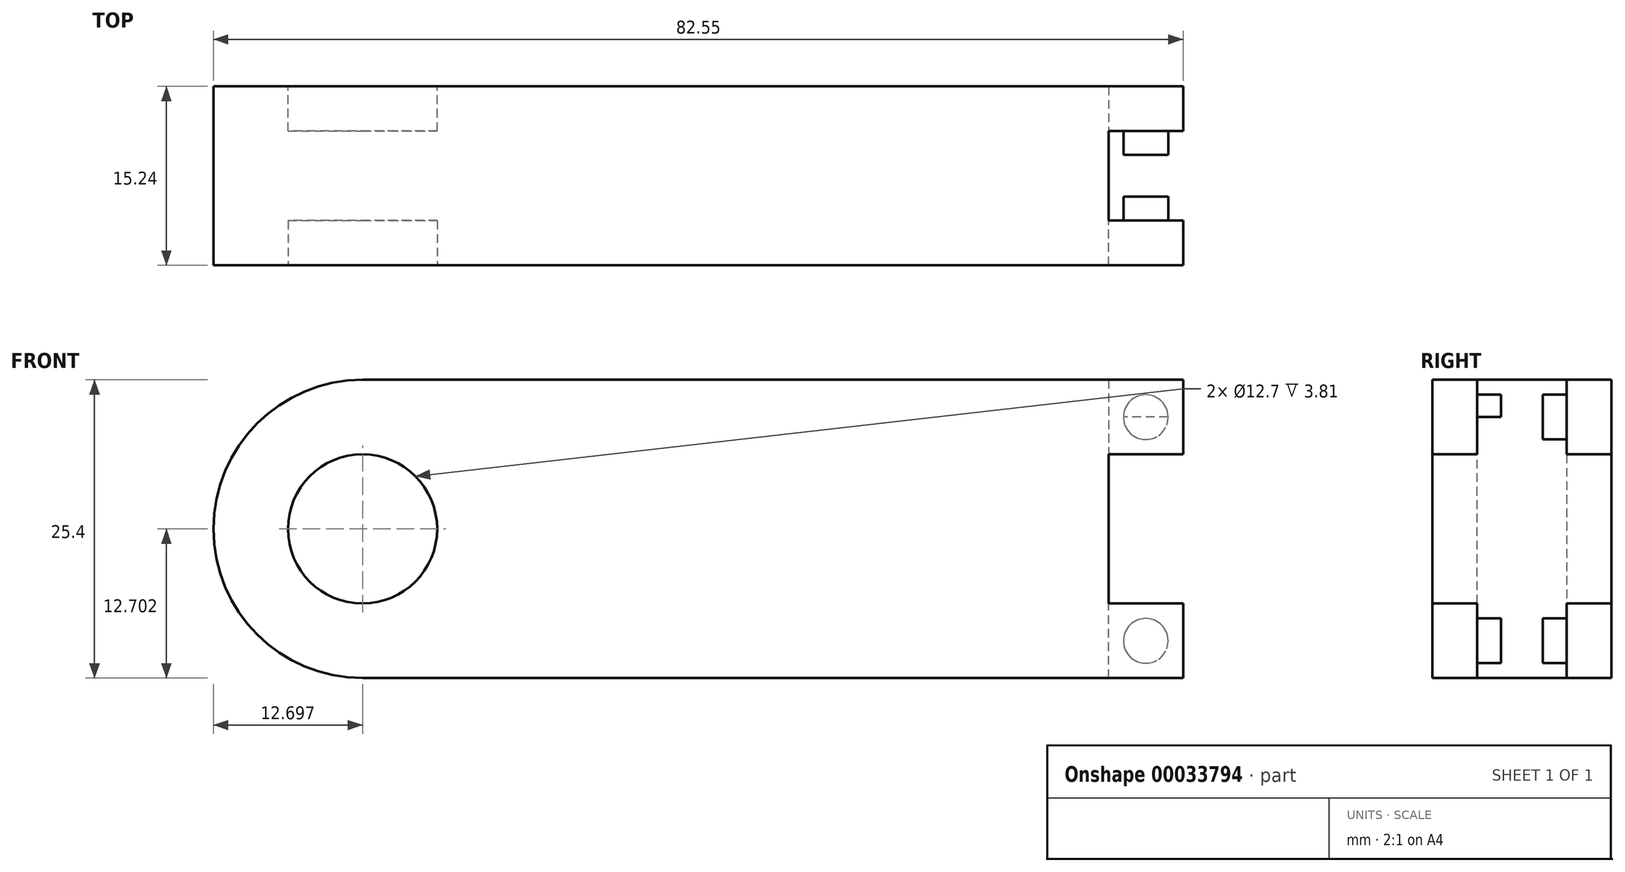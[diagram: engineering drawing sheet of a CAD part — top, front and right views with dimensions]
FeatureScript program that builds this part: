
annotation { "Feature Type Name" : "Feature", "Feature Type Description" : "" }
export const myFeature = defineFeature(function(context is Context, id is Id, definition is map)
    precondition{}
    {
        {
            var Q0;
            Q0=qCreatedBy(makeId("Front.planeOp"),FACE);
            var sketch = newSketch(context, id + "F0", { "sketchPlane" : qUnion([Q0])});
            skLineSegment(sketch, "E0.bottom", {"start": v(16.69, 10.43) * mm, "end": v(92.89, 10.43) * mm});
            skLineSegment(sketch, "E0.top", {"start": v(16.69, -14.97) * mm, "end": v(92.89, -14.97) * mm});
            skLineSegment(sketch, "E0.left", {"start": v(16.69, 10.43) * mm, "end": v(16.69, -14.97) * mm});
            skLineSegment(sketch, "E0.right", {"start": v(92.89, 10.43) * mm, "end": v(92.89, -14.97) * mm});
            skCircle(sketch, "E1", {"center": v(29.39, -2.27) * mm, "radius": 12.7 * mm});
            skCircle(sketch, "E2", {"center": v(29.39, -2.27) * mm, "radius": 6.35 * mm});
            skSolve(sketch);
        }
        {
            var Q0;
            Q0=makeQuery(id+"F0.imprint","IMPRINT",FACE,{"disambiguationData":[TD([[makeQuery(id+"F0.imprint","IMPRINT",EDGE,{"derivedFrom":sQuery(id+"F0.wireOp",EDGE,"E2")}),-1.0]])]});
            var Q1;
            Q1=makeQuery(id+"F0.imprint","IMPRINT",FACE,{"disambiguationData":[TD([[makeQuery(id+"F0.imprint","IMPRINT",EDGE,{"derivedFrom":sQuery(id+"F0.wireOp",EDGE,"E2")}),1.0]])]});
            var Q2;
            {var subQ5=sQuery(id+"F0.wireOp",EDGE,"E0.right");Q2=makeQuery(id+"F0.imprint","IMPRINT",FACE,{"disambiguationData":[TD([[makeQuery(id+"F0.imprint","IMPRINT",EDGE,{"derivedFrom":subQ5}),-1.0]])]});}
            extrude(context, id + "F1", {"entities" : qUnion([Q0, Q1, Q2]), "oppositeDirection" : true, "depth" : 25.4 * mm});
        }
        {
            var Q0;
            Q0=makeQuery(id+"F1.opExtrude","CAP_FACE",FACE,{"disambiguationData":[OSD([sQuery(id+"F0.wireOp",EDGE,"E0.bottom"),sQuery(id+"F0.wireOp",EDGE,"E0.top"),sQuery(id+"F0.wireOp",EDGE,"E0.right"),sQuery(id+"F0.wireOp",EDGE,"E1")])],"isStart":false});
            var sketch = newSketch(context, id + "F2", { "sketchPlane" : qUnion([Q0])});
            skCircle(sketch, "E3", {"center": v(-29.39, -2.27) * mm, "radius": 12.7 * mm});
            skCircle(sketch, "E4", {"center": v(-29.39, -2.27) * mm, "radius": 6.35 * mm});
            skSolve(sketch);
        }
        {
            var Q0;
            {var subQ0=sQuery(id+"F2.wireOp",EDGE,"E3");Q0=makeQuery(id+"F2.imprint","IMPRINT",FACE,{"disambiguationData":[TD([[makeQuery(id+"F2.imprint","IMPRINT",EDGE,{"disambiguationData":[OD(0.0)],"derivedFrom":subQ0}),1.0]])]});}
            var Q1;
            Q1=makeQuery(id+"F2.imprint","IMPRINT",FACE,{"disambiguationData":[TD([[makeQuery(id+"F2.imprint","IMPRINT",EDGE,{"derivedFrom":sQuery(id+"F2.wireOp",EDGE,"E4")}),1.0]])]});
            extrude(context, id + "F3", {"entities" : qUnion([Q0, Q1]), "operationType" : NewBodyOperationType.REMOVE, "endBound" : BoundingType.UP_TO_NEXT, "oppositeDirection" : true, "depth" : 25.4 * mm});
        }
        {
            var Q0;
            {var subQ0=sQuery(id+"F2.wireOp",EDGE,"E3");Q0=makeQuery(id+"F2.imprint","IMPRINT",FACE,{"disambiguationData":[TD([[makeQuery(id+"F2.imprint","IMPRINT",EDGE,{"disambiguationData":[OD(0.0)],"derivedFrom":subQ0}),1.0]])]});}
            extrude(context, id + "F4", {"entities" : qUnion([Q0]), "operationType" : NewBodyOperationType.ADD, "oppositeDirection" : true, "depth" : 5.08 * mm});
        }
        {
            var Q0;
            Q0=makeQuery(id+"F2.imprint","IMPRINT",FACE,{"disambiguationData":[TD([[makeQuery(id+"F2.imprint","IMPRINT",EDGE,{"derivedFrom":sQuery(id+"F2.wireOp",EDGE,"E4")}),1.0]])]});
            extrude(context, id + "F5", {"entities" : qUnion([Q0]), "operationType" : NewBodyOperationType.ADD, "oppositeDirection" : true, "depth" : 8.9 * mm});
        }
        {
            var Q0;
            {var subQ0=sQuery(id+"F2.wireOp",EDGE,"E3");Q0=makeQuery(id+"F2.imprint","IMPRINT",FACE,{"disambiguationData":[TD([[makeQuery(id+"F2.imprint","IMPRINT",EDGE,{"disambiguationData":[OD(0.0)],"derivedFrom":subQ0}),1.0]])]});}
            var Q1;
            Q1=makeQuery(id+"F2.imprint","IMPRINT",FACE,{"disambiguationData":[TD([[makeQuery(id+"F2.imprint","IMPRINT",EDGE,{"derivedFrom":sQuery(id+"F2.wireOp",EDGE,"E4")}),1.0]])]});
            extrude(context, id + "F6", {"entities" : qUnion([Q0, Q1]), "operationType" : NewBodyOperationType.ADD, "oppositeDirection" : true, "depth" : 20.32 * mm});
        }
        {
            var Q0;
            Q0=makeQuery(id+"F1.opExtrude","CAP_FACE",FACE,{"disambiguationData":[OSD([sQuery(id+"F0.wireOp",EDGE,"E0.bottom"),sQuery(id+"F0.wireOp",EDGE,"E0.top"),sQuery(id+"F0.wireOp",EDGE,"E0.right"),sQuery(id+"F0.wireOp",EDGE,"E1")])],"isStart":true});
            extrude(context, id + "F7", {"entities" : qUnion([Q0]), "operationType" : NewBodyOperationType.REMOVE, "oppositeDirection" : true, "depth" : 10.16 * mm});
        }
        {
            var Q0;
            Q0=makeQuery(id+"F6.opExtrude","CAP_FACE",FACE,{"disambiguationData":[OSD([sQuery(id+"F2.wireOp",EDGE,"E3")])],"isStart":false});
            extrude(context, id + "F8", {"entities" : qUnion([Q0]), "operationType" : NewBodyOperationType.REMOVE, "oppositeDirection" : true, "depth" : 5.08 * mm});
        }
        {
            var Q0;
            Q0=makeQuery(id+"F0.imprint","IMPRINT",FACE,{"disambiguationData":[TD([[makeQuery(id+"F0.imprint","IMPRINT",EDGE,{"derivedFrom":sQuery(id+"F0.wireOp",EDGE,"E2")}),1.0]])]});
            extrude(context, id + "F9", {"entities" : qUnion([Q0]), "operationType" : NewBodyOperationType.REMOVE, "oppositeDirection" : true, "depth" : 13.97 * mm});
        }
        {
            var Q0;
            Q0=makeQuery(id+"F2.imprint","IMPRINT",FACE,{"disambiguationData":[TD([[makeQuery(id+"F2.imprint","IMPRINT",EDGE,{"derivedFrom":sQuery(id+"F2.wireOp",EDGE,"E4")}),1.0]])]});
            extrude(context, id + "F10", {"entities" : qUnion([Q0]), "operationType" : NewBodyOperationType.REMOVE, "oppositeDirection" : true, "depth" : 3.8 * mm});
        }
        {
            var Q0;
            Q0=makeQuery(id+"F1.opExtrude","SWEPT_FACE",FACE,{"disambiguationData":[OSD([sQuery(id+"F0.wireOp",EDGE,"E0.right")])]});
            var sketch = newSketch(context, id + "F11", { "sketchPlane" : qUnion([Q0])});
            skLineSegment(sketch, "E5.bottom", {"start": v(10.16, 10.43) * mm, "end": v(13.97, 10.43) * mm});
            skLineSegment(sketch, "E5.top", {"start": v(10.16, 4.08) * mm, "end": v(13.97, 4.08) * mm});
            skLineSegment(sketch, "E5.left", {"start": v(10.16, 10.43) * mm, "end": v(10.16, 4.08) * mm});
            skLineSegment(sketch, "E5.right", {"start": v(13.97, 10.43) * mm, "end": v(13.97, 4.08) * mm});
            skLineSegment(sketch, "E6.bottom", {"start": v(25.4, 10.43) * mm, "end": v(21.59, 10.43) * mm});
            skLineSegment(sketch, "E6.top", {"start": v(25.4, 4.08) * mm, "end": v(21.59, 4.08) * mm});
            skLineSegment(sketch, "E6.left", {"start": v(25.4, 10.43) * mm, "end": v(25.4, 4.08) * mm});
            skLineSegment(sketch, "E6.right", {"start": v(21.59, 10.43) * mm, "end": v(21.59, 4.08) * mm});
            skLineSegment(sketch, "E7.bottom", {"start": v(10.16, -14.97) * mm, "end": v(13.97, -14.97) * mm});
            skLineSegment(sketch, "E7.top", {"start": v(10.16, -8.62) * mm, "end": v(13.97, -8.62) * mm});
            skLineSegment(sketch, "E7.left", {"start": v(10.16, -14.97) * mm, "end": v(10.16, -8.62) * mm});
            skLineSegment(sketch, "E7.right", {"start": v(13.97, -14.97) * mm, "end": v(13.97, -8.62) * mm});
            skLineSegment(sketch, "E8.bottom", {"start": v(25.4, -14.97) * mm, "end": v(21.59, -14.97) * mm});
            skLineSegment(sketch, "E8.top", {"start": v(25.4, -8.62) * mm, "end": v(21.59, -8.62) * mm});
            skLineSegment(sketch, "E8.left", {"start": v(25.4, -14.97) * mm, "end": v(25.4, -8.62) * mm});
            skLineSegment(sketch, "E8.right", {"start": v(21.59, -14.97) * mm, "end": v(21.59, -8.62) * mm});
            skSolve(sketch);
        }
        {
            var Q0;
            Q0=makeQuery(id+"F11.imprint","IMPRINT",FACE,{"disambiguationData":[TD([[makeQuery(id+"F11.imprint","IMPRINT",EDGE,{"derivedFrom":sQuery(id+"F11.wireOp",EDGE,"E5.bottom")}),1.0]])]});
            var Q1;
            Q1=makeQuery(id+"F11.imprint","IMPRINT",FACE,{"disambiguationData":[TD([[makeQuery(id+"F11.imprint","IMPRINT",EDGE,{"derivedFrom":sQuery(id+"F11.wireOp",EDGE,"E6.bottom")}),1.0]])]});
            var Q2;
            Q2=makeQuery(id+"F11.imprint","IMPRINT",FACE,{"disambiguationData":[TD([[makeQuery(id+"F11.imprint","IMPRINT",EDGE,{"derivedFrom":sQuery(id+"F11.wireOp",EDGE,"E8.bottom")}),-1.0]])]});
            var Q3;
            Q3=makeQuery(id+"F11.imprint","IMPRINT",FACE,{"disambiguationData":[TD([[makeQuery(id+"F11.imprint","IMPRINT",EDGE,{"derivedFrom":sQuery(id+"F11.wireOp",EDGE,"E7.bottom")}),-1.0]])]});
            extrude(context, id + "F12", {"entities" : qUnion([Q0, Q1, Q2, Q3]), "operationType" : NewBodyOperationType.ADD, "depth" : 6.35 * mm});
        }
        {
            var Q0;
            Q0=makeQuery(id+"F12.opExtrude","SWEPT_FACE",FACE,{"disambiguationData":[OSD([sQuery(id+"F11.wireOp",EDGE,"E5.right")])]});
            var sketch = newSketch(context, id + "F13", { "sketchPlane" : qUnion([Q0])});
            skCircle(sketch, "E9", {"center": v(-96.06, 7.26) * mm, "radius": 1.9 * mm});
            skLineSegment(sketch, "E10", {"start": v(-99.24, 7.26) * mm, "end": v(-92.89, 7.26) * mm});
            skLineSegment(sketch, "E11", {"start": v(-96.06, 10.43) * mm, "end": v(-96.06, 4.08) * mm});
            skSolve(sketch);
        }
        {
            var Q0;
            Q0=makeQuery(id+"F12.opExtrude","SWEPT_FACE",FACE,{"disambiguationData":[OSD([sQuery(id+"F11.wireOp",EDGE,"E6.right")])]});
            var sketch = newSketch(context, id + "F14", { "sketchPlane" : qUnion([Q0])});
            skCircle(sketch, "E12", {"center": v(96.06, 7.26) * mm, "radius": 1.9 * mm});
            skLineSegment(sketch, "E13", {"start": v(99.24, 7.26) * mm, "end": v(92.89, 7.26) * mm});
            skLineSegment(sketch, "E14", {"start": v(96.06, 10.43) * mm, "end": v(96.06, 4.08) * mm});
            skSolve(sketch);
        }
        {
            var Q0;
            Q0=makeQuery(id+"F12.opExtrude","SWEPT_FACE",FACE,{"disambiguationData":[OSD([sQuery(id+"F11.wireOp",EDGE,"E7.right")])]});
            var sketch = newSketch(context, id + "F15", { "sketchPlane" : qUnion([Q0])});
            skLineSegment(sketch, "E15", {"start": v(-99.24, -11.8) * mm, "end": v(-92.89, -11.8) * mm});
            skLineSegment(sketch, "E16", {"start": v(-96.06, -8.62) * mm, "end": v(-96.06, -14.97) * mm});
            skCircle(sketch, "E17", {"center": v(-96.06, -11.8) * mm, "radius": 1.9 * mm});
            skSolve(sketch);
        }
        {
            var Q0;
            Q0=makeQuery(id+"F12.opExtrude","SWEPT_FACE",FACE,{"disambiguationData":[OSD([sQuery(id+"F11.wireOp",EDGE,"E8.right")])]});
            var sketch = newSketch(context, id + "F16", { "sketchPlane" : qUnion([Q0])});
            skLineSegment(sketch, "E18", {"start": v(96.06, -14.97) * mm, "end": v(96.06, -8.62) * mm});
            skLineSegment(sketch, "E19", {"start": v(99.24, -11.8) * mm, "end": v(92.89, -11.8) * mm});
            skCircle(sketch, "E20", {"center": v(96.06, -11.8) * mm, "radius": 1.9 * mm});
            skSolve(sketch);
        }
        {
            var Q0;
            {var subQ1=sQuery(id+"F15.wireOp",EDGE,"E16");var subQ3=sQuery(id+"F15.wireOp",EDGE,"E15");var subQ5=makeQuery(id+"F15.imprint","INTERSECT",VERTEX,{"derivedFrom":[subQ3,subQ1]});Q0=makeQuery(id+"F15.imprint","IMPRINT",FACE,{"disambiguationData":[TD([[makeQuery(id+"F15.imprint","IMPRINT",EDGE,{"disambiguationData":[TD([[subQ5,-1.0]])],"derivedFrom":subQ3}),1.0]])]});}
            var Q1;
            {var subQ0=sQuery(id+"F15.wireOp",EDGE,"E17");var subQ3=sQuery(id+"F15.wireOp",EDGE,"E15");var subQ4=makeQuery(id+"F15.imprint","INTERSECT",VERTEX,{"disambiguationData":[OD(0.0)],"derivedFrom":[subQ3,subQ0]});Q1=makeQuery(id+"F15.imprint","IMPRINT",FACE,{"disambiguationData":[TD([[makeQuery(id+"F15.imprint","IMPRINT",EDGE,{"disambiguationData":[TD([[subQ4,-1.0]])],"derivedFrom":subQ3}),1.0]])]});}
            var Q2;
            {var subQ0=sQuery(id+"F15.wireOp",EDGE,"E17");var subQ3=sQuery(id+"F15.wireOp",EDGE,"E15");var subQ4=makeQuery(id+"F15.imprint","INTERSECT",VERTEX,{"disambiguationData":[OD(0.0)],"derivedFrom":[subQ3,subQ0]});Q2=makeQuery(id+"F15.imprint","IMPRINT",FACE,{"disambiguationData":[TD([[makeQuery(id+"F15.imprint","IMPRINT",EDGE,{"disambiguationData":[TD([[subQ4,-1.0]])],"derivedFrom":subQ3}),-1.0]])]});}
            var Q3;
            {var subQ1=sQuery(id+"F15.wireOp",EDGE,"E16");var subQ3=sQuery(id+"F15.wireOp",EDGE,"E15");var subQ5=makeQuery(id+"F15.imprint","INTERSECT",VERTEX,{"derivedFrom":[subQ3,subQ1]});Q3=makeQuery(id+"F15.imprint","IMPRINT",FACE,{"disambiguationData":[TD([[makeQuery(id+"F15.imprint","IMPRINT",EDGE,{"disambiguationData":[TD([[subQ5,-1.0]])],"derivedFrom":subQ3}),-1.0]])]});}
            var Q4;
            {var subQ0=sQuery(id+"F13.wireOp",EDGE,"E11");var subQ3=sQuery(id+"F13.wireOp",EDGE,"E9");var subQ4=makeQuery(id+"F13.imprint","INTERSECT",VERTEX,{"disambiguationData":[OD(0.0)],"derivedFrom":[subQ3,subQ0]});Q4=makeQuery(id+"F13.imprint","IMPRINT",FACE,{"disambiguationData":[TD([[makeQuery(id+"F13.imprint","IMPRINT",EDGE,{"disambiguationData":[TD([[subQ4,-1.0]])],"derivedFrom":subQ3}),1.0]])]});}
            var Q5;
            {var subQ0=sQuery(id+"F13.wireOp",EDGE,"E11");var subQ3=sQuery(id+"F13.wireOp",EDGE,"E9");var subQ4=makeQuery(id+"F13.imprint","INTERSECT",VERTEX,{"disambiguationData":[OD(0.0)],"derivedFrom":[subQ3,subQ0]});Q5=makeQuery(id+"F13.imprint","IMPRINT",FACE,{"disambiguationData":[TD([[makeQuery(id+"F13.imprint","IMPRINT",EDGE,{"disambiguationData":[TD([[subQ4,1.0]])],"derivedFrom":subQ3}),1.0]])]});}
            var Q6;
            {var subQ1=sQuery(id+"F13.wireOp",EDGE,"E10");var subQ3=sQuery(id+"F13.wireOp",EDGE,"E9");var subQ5=makeQuery(id+"F13.imprint","INTERSECT",VERTEX,{"disambiguationData":[OD(1.0)],"derivedFrom":[subQ3,subQ1]});Q6=makeQuery(id+"F13.imprint","IMPRINT",FACE,{"disambiguationData":[TD([[makeQuery(id+"F13.imprint","IMPRINT",EDGE,{"disambiguationData":[TD([[subQ5,-1.0]])],"derivedFrom":subQ3}),1.0]])]});}
            var Q7;
            {var subQ1=sQuery(id+"F13.wireOp",EDGE,"E10");var subQ3=sQuery(id+"F13.wireOp",EDGE,"E9");var subQ5=makeQuery(id+"F13.imprint","INTERSECT",VERTEX,{"disambiguationData":[OD(0.0)],"derivedFrom":[subQ3,subQ1]});Q7=makeQuery(id+"F13.imprint","IMPRINT",FACE,{"disambiguationData":[TD([[makeQuery(id+"F13.imprint","IMPRINT",EDGE,{"disambiguationData":[TD([[subQ5,1.0]])],"derivedFrom":subQ3}),1.0]])]});}
            extrude(context, id + "F17", {"entities" : qUnion([Q0, Q1, Q2, Q3, Q4, Q5, Q6, Q7]), "operationType" : NewBodyOperationType.ADD, "depth" : 2.03 * mm});
        }
        {
            var Q0;
            {var subQ0=sQuery(id+"F14.wireOp",EDGE,"E14");var subQ3=sQuery(id+"F14.wireOp",EDGE,"E12");var subQ4=makeQuery(id+"F14.imprint","INTERSECT",VERTEX,{"disambiguationData":[OD(0.0)],"derivedFrom":[subQ3,subQ0]});Q0=makeQuery(id+"F14.imprint","IMPRINT",FACE,{"disambiguationData":[TD([[makeQuery(id+"F14.imprint","IMPRINT",EDGE,{"disambiguationData":[TD([[subQ4,-1.0]])],"derivedFrom":subQ3}),1.0]])]});}
            var Q1;
            {var subQ0=sQuery(id+"F14.wireOp",EDGE,"E14");var subQ3=sQuery(id+"F14.wireOp",EDGE,"E12");var subQ4=makeQuery(id+"F14.imprint","INTERSECT",VERTEX,{"disambiguationData":[OD(0.0)],"derivedFrom":[subQ3,subQ0]});Q1=makeQuery(id+"F14.imprint","IMPRINT",FACE,{"disambiguationData":[TD([[makeQuery(id+"F14.imprint","IMPRINT",EDGE,{"disambiguationData":[TD([[subQ4,1.0]])],"derivedFrom":subQ3}),1.0]])]});}
            var Q2;
            {var subQ1=sQuery(id+"F14.wireOp",EDGE,"E13");var subQ3=sQuery(id+"F14.wireOp",EDGE,"E12");var subQ5=makeQuery(id+"F14.imprint","INTERSECT",VERTEX,{"disambiguationData":[OD(0.0)],"derivedFrom":[subQ3,subQ1]});Q2=makeQuery(id+"F14.imprint","IMPRINT",FACE,{"disambiguationData":[TD([[makeQuery(id+"F14.imprint","IMPRINT",EDGE,{"disambiguationData":[TD([[subQ5,1.0]])],"derivedFrom":subQ3}),1.0]])]});}
            var Q3;
            {var subQ1=sQuery(id+"F14.wireOp",EDGE,"E13");var subQ3=sQuery(id+"F14.wireOp",EDGE,"E12");var subQ5=makeQuery(id+"F14.imprint","INTERSECT",VERTEX,{"disambiguationData":[OD(1.0)],"derivedFrom":[subQ3,subQ1]});Q3=makeQuery(id+"F14.imprint","IMPRINT",FACE,{"disambiguationData":[TD([[makeQuery(id+"F14.imprint","IMPRINT",EDGE,{"disambiguationData":[TD([[subQ5,-1.0]])],"derivedFrom":subQ3}),1.0]])]});}
            var Q4;
            {var subQ1=sQuery(id+"F16.wireOp",EDGE,"E19");var subQ3=sQuery(id+"F16.wireOp",EDGE,"E18");var subQ5=makeQuery(id+"F16.imprint","INTERSECT",VERTEX,{"derivedFrom":[subQ3,subQ1]});Q4=makeQuery(id+"F16.imprint","IMPRINT",FACE,{"disambiguationData":[TD([[makeQuery(id+"F16.imprint","IMPRINT",EDGE,{"disambiguationData":[TD([[subQ5,-1.0]])],"derivedFrom":subQ3}),1.0]])]});}
            var Q5;
            {var subQ1=sQuery(id+"F16.wireOp",EDGE,"E19");var subQ3=sQuery(id+"F16.wireOp",EDGE,"E18");var subQ5=makeQuery(id+"F16.imprint","INTERSECT",VERTEX,{"derivedFrom":[subQ3,subQ1]});Q5=makeQuery(id+"F16.imprint","IMPRINT",FACE,{"disambiguationData":[TD([[makeQuery(id+"F16.imprint","IMPRINT",EDGE,{"disambiguationData":[TD([[subQ5,-1.0]])],"derivedFrom":subQ3}),-1.0]])]});}
            var Q6;
            {var subQ0=sQuery(id+"F16.wireOp",EDGE,"E20");var subQ3=sQuery(id+"F16.wireOp",EDGE,"E18");var subQ4=makeQuery(id+"F16.imprint","INTERSECT",VERTEX,{"disambiguationData":[OD(0.0)],"derivedFrom":[subQ3,subQ0]});Q6=makeQuery(id+"F16.imprint","IMPRINT",FACE,{"disambiguationData":[TD([[makeQuery(id+"F16.imprint","IMPRINT",EDGE,{"disambiguationData":[TD([[subQ4,-1.0]])],"derivedFrom":subQ3}),-1.0]])]});}
            var Q7;
            {var subQ0=sQuery(id+"F16.wireOp",EDGE,"E20");var subQ3=sQuery(id+"F16.wireOp",EDGE,"E18");var subQ4=makeQuery(id+"F16.imprint","INTERSECT",VERTEX,{"disambiguationData":[OD(0.0)],"derivedFrom":[subQ3,subQ0]});Q7=makeQuery(id+"F16.imprint","IMPRINT",FACE,{"disambiguationData":[TD([[makeQuery(id+"F16.imprint","IMPRINT",EDGE,{"disambiguationData":[TD([[subQ4,-1.0]])],"derivedFrom":subQ3}),1.0]])]});}
            extrude(context, id + "F18", {"entities" : qUnion([Q0, Q1, Q2, Q3, Q4, Q5, Q6, Q7]), "operationType" : NewBodyOperationType.ADD, "depth" : 2.03 * mm});
        }
    });
